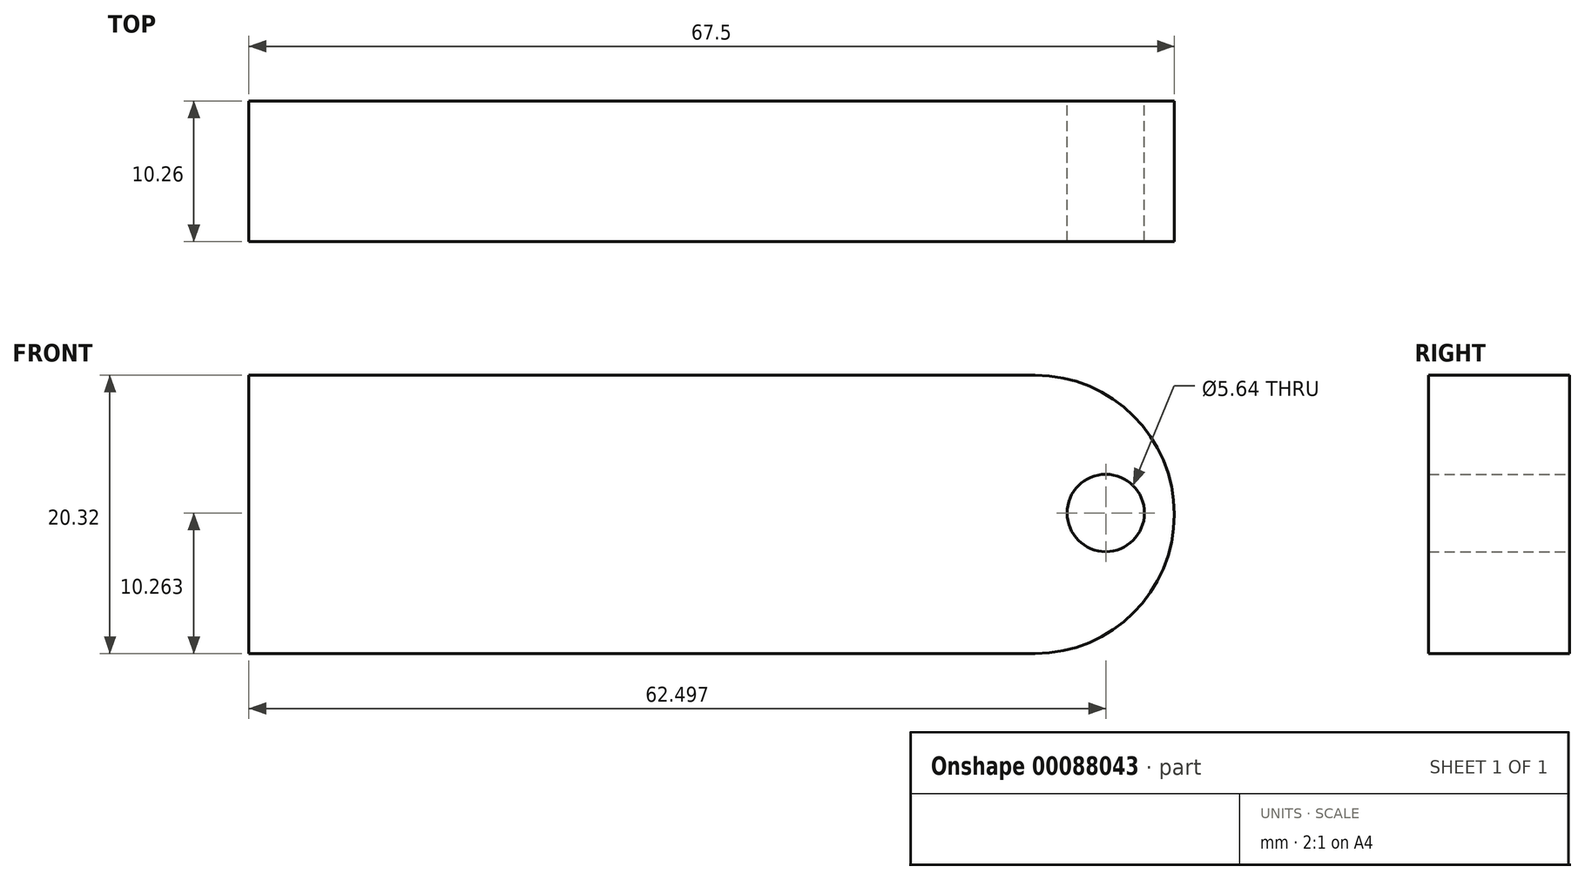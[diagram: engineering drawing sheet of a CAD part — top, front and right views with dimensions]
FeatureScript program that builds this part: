
annotation { "Feature Type Name" : "Feature", "Feature Type Description" : "" }
export const myFeature = defineFeature(function(context is Context, id is Id, definition is map)
    precondition{}
    {
        {
            var Q0;
            Q0=qCreatedBy(makeId("Front.planeOp"),FACE);
            var sketch = newSketch(context, id + "F0", { "sketchPlane" : qUnion([Q0])});
            skLineSegment(sketch, "E0.bottom", {"start": v(0, 0) * mm, "end": v(-57.34, 0) * mm});
            skLineSegment(sketch, "E0.top", {"start": v(0, 20.32) * mm, "end": v(-57.34, 20.32) * mm});
            skLineSegment(sketch, "E0.left", {"start": v(0, 0) * mm, "end": v(0, 20.32) * mm});
            skLineSegment(sketch, "E0.right", {"start": v(-57.34, 0) * mm, "end": v(-57.34, 20.32) * mm});
            skArc(sketch, "E1", {"start": v(0, 0) * mm, "mid": v(10.16, 10.16) * mm, "end": v(0, 20.32) * mm});
            skCircle(sketch, "E2", {"center": v(5.16, 10.26) * mm, "radius": 2.82 * mm});
            skSolve(sketch);
        }
        {
            var Q0;
            Q0=makeQuery(id+"F0.imprint","IMPRINT",FACE,{"disambiguationData":[TD([[makeQuery(id+"F0.imprint","IMPRINT",EDGE,{"derivedFrom":sQuery(id+"F0.wireOp",EDGE,"E0.bottom")}),-1.0]])]});
            var Q1;
            Q1=makeQuery(id+"F0.imprint","IMPRINT",FACE,{"disambiguationData":[TD([[makeQuery(id+"F0.imprint","IMPRINT",EDGE,{"derivedFrom":sQuery(id+"F0.wireOp",EDGE,"E0.left")}),-1.0]])]});
            extrude(context, id + "F1", {"entities" : qUnion([Q0, Q1]), "depth" : 10.26 * mm});
        }
    });
